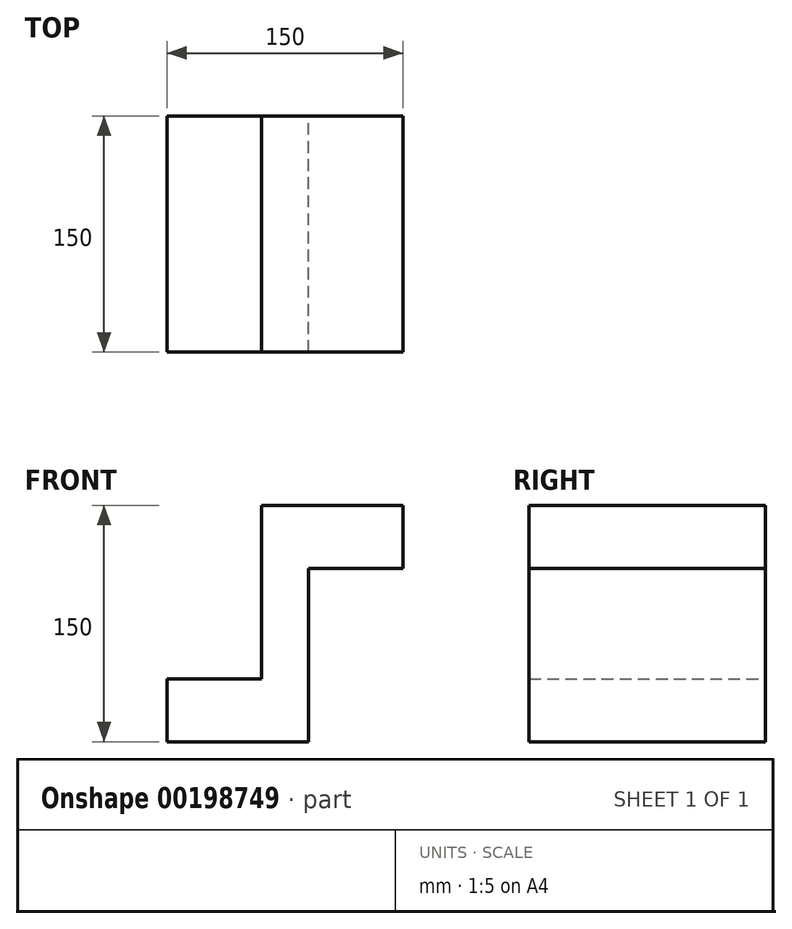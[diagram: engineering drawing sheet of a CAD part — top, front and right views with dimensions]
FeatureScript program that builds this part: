
annotation { "Feature Type Name" : "Feature", "Feature Type Description" : "" }
export const myFeature = defineFeature(function(context is Context, id is Id, definition is map)
    precondition{}
    {
        {
            var Q0;
            Q0=qCreatedBy(makeId("Front.planeOp"),FACE);
            var sketch = newSketch(context, id + "F0", { "sketchPlane" : qUnion([Q0])});
            skLineSegment(sketch, "E0.bottom", {"start": v(75, 75) * mm, "end": v(-15, 75) * mm});
            skLineSegment(sketch, "E0.top", {"start": v(15, -75) * mm, "end": v(-75, -75) * mm});
            skLineSegment(sketch, "E0.left", {"start": v(75, 75) * mm, "end": v(75, 35) * mm});
            skPoint(sketch, "E0.middle", {"position": v(0, 0) * mm});
            skLineSegment(sketch, "E1.top", {"start": v(75, 35) * mm, "end": v(15, 35) * mm});
            skLineSegment(sketch, "E1.right", {"start": v(15, -75) * mm, "end": v(15, 35) * mm});
            skLineSegment(sketch, "E2.top", {"start": v(-75, -35) * mm, "end": v(-15, -35) * mm});
            skLineSegment(sketch, "E2.right", {"start": v(-15, 75) * mm, "end": v(-15, -35) * mm});
            skLineSegment(sketch, "E3", {"start": v(-75, -35) * mm, "end": v(-75, -75) * mm});
            skSolve(sketch);
        }
        {
            var Q0;
            Q0 = qSketchRegion(id + "F0", true);
            extrude(context, id + "F1", {"entities" : qUnion([Q0]), "endBound" : BoundingType.SYMMETRIC, "depth" : 150 * mm});
        }
    });
